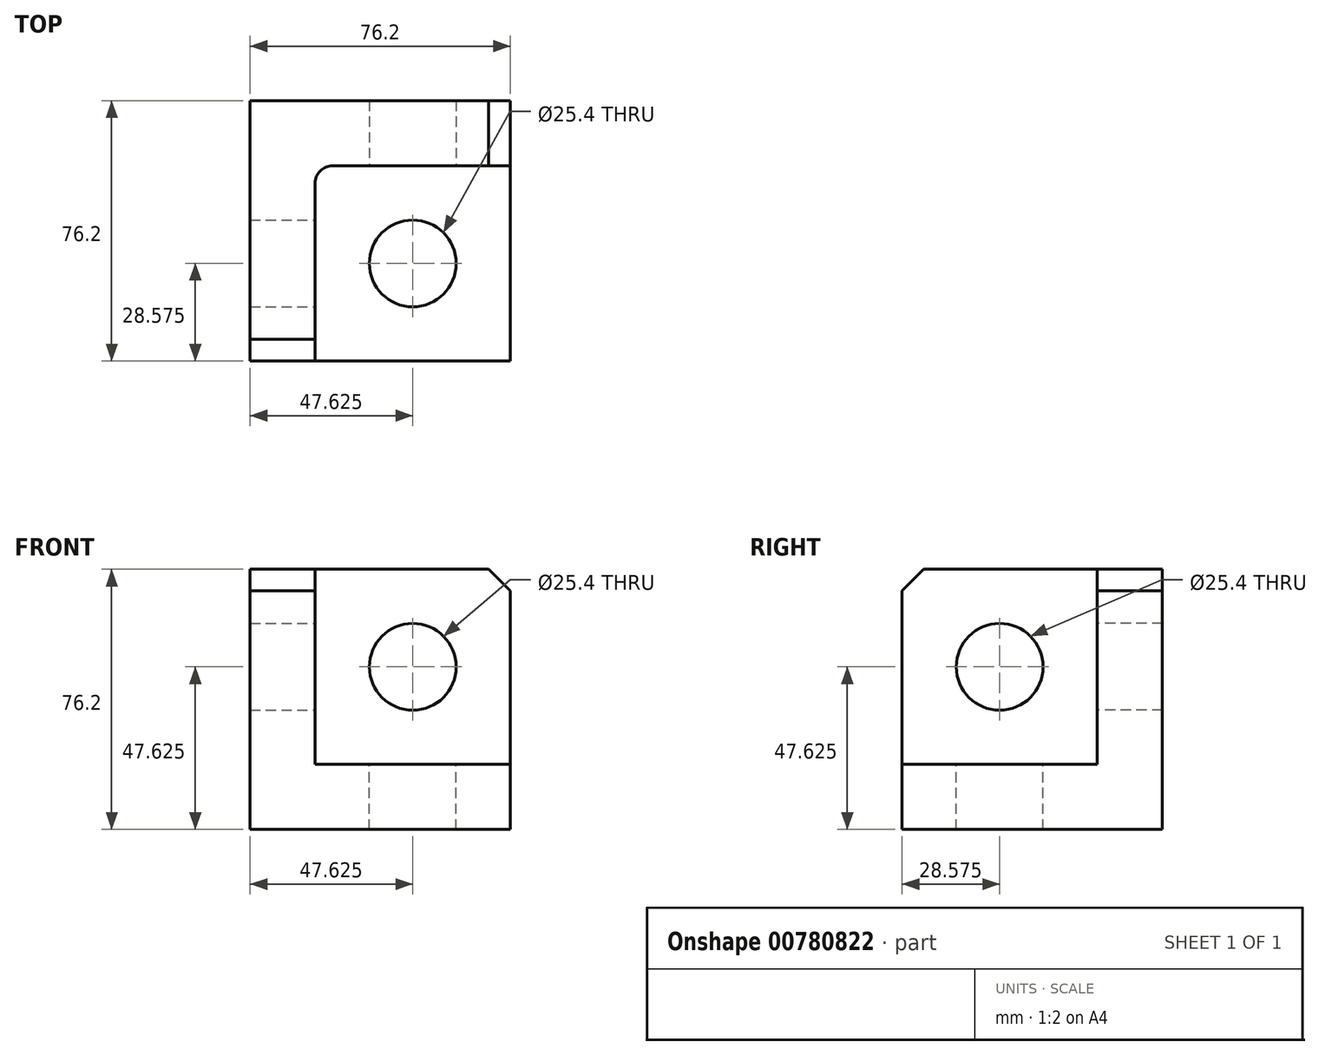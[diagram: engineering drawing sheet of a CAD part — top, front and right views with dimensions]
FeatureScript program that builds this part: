
annotation { "Feature Type Name" : "Feature", "Feature Type Description" : "" }
export const myFeature = defineFeature(function(context is Context, id is Id, definition is map)
    precondition{}
    {
        {
            var Q0;
            Q0=qCreatedBy(makeId("Front.planeOp"),FACE);
            var sketch = newSketch(context, id + "F0", { "sketchPlane" : qUnion([Q0])});
            skLineSegment(sketch, "E0.bottom", {"start": v(-38.1, 38.1) * mm, "end": v(38.1, 38.1) * mm});
            skLineSegment(sketch, "E0.top", {"start": v(-38.1, -38.1) * mm, "end": v(38.1, -38.1) * mm});
            skLineSegment(sketch, "E0.left", {"start": v(-38.1, 38.1) * mm, "end": v(-38.1, -38.1) * mm});
            skLineSegment(sketch, "E0.right", {"start": v(38.1, 38.1) * mm, "end": v(38.1, -38.1) * mm});
            skPoint(sketch, "E0.middle", {"position": v(0, 0) * mm});
            skSolve(sketch);
        }
        {
            var Q0;
            Q0=makeQuery(id+"F0.imprint","IMPRINT",FACE,{"disambiguationData":[TD([[makeQuery(id+"F0.imprint","IMPRINT",EDGE,{"derivedFrom":sQuery(id+"F0.wireOp",EDGE,"E0.bottom")}),-1.0]])]});
            extrude(context, id + "F1", {"entities" : qUnion([Q0]), "depth" : 76.2 * mm, "offsetDistance" : 25.4 * mm});
        }
        {
            var Q0;
            Q0=makeQuery(id+"F1.opExtrude","CAP_FACE",FACE,{"disambiguationData":[OSD([sQuery(id+"F0.wireOp",EDGE,"E0.bottom"),sQuery(id+"F0.wireOp",EDGE,"E0.top"),sQuery(id+"F0.wireOp",EDGE,"E0.left"),sQuery(id+"F0.wireOp",EDGE,"E0.right")])],"isStart":false});
            var sketch = newSketch(context, id + "F2", { "sketchPlane" : qUnion([Q0])});
            skLineSegment(sketch, "E1.bottom", {"start": v(38.1, 38.1) * mm, "end": v(-19.05, 38.1) * mm});
            skLineSegment(sketch, "E1.top", {"start": v(38.1, -19.05) * mm, "end": v(-19.05, -19.05) * mm});
            skLineSegment(sketch, "E1.left", {"start": v(38.1, 38.1) * mm, "end": v(38.1, -19.05) * mm});
            skLineSegment(sketch, "E1.right", {"start": v(-19.05, 38.1) * mm, "end": v(-19.05, -19.05) * mm});
            skSolve(sketch);
        }
        {
            var Q0;
            Q0=makeQuery(id+"F2.imprint","IMPRINT",FACE,{"disambiguationData":[TD([[makeQuery(id+"F2.imprint","IMPRINT",EDGE,{"derivedFrom":sQuery(id+"F2.wireOp",EDGE,"E1.bottom")}),-1.0]])]});
            extrude(context, id + "F3", {"entities" : qUnion([Q0]), "operationType" : NewBodyOperationType.REMOVE, "oppositeDirection" : true, "depth" : 57.15 * mm, "offsetDistance" : 25.4 * mm});
        }
        {
            var Q0;
            Q0=makeQuery(id+"F1.opExtrude","CAP_EDGE",EDGE,{"disambiguationData":[OSD([sQuery(id+"F0.wireOp",EDGE,"E0.bottom")])],"isStart":false});
            chamfer(context, id + "F4", {"entities" : qUnion([Q0]), "width" : 6.35 * mm, "tangentPropagation" : true});
        }
        {
            var Q0;
            Q0=makeQuery(id+"F1.opExtrude","SWEPT_EDGE",EDGE,{"disambiguationData":[OSD([sQuery(id+"F0.wireOp",EDGE,"E0.bottom"),sQuery(id+"F0.wireOp",EDGE,"E0.right")])]});
            chamfer(context, id + "F5", {"entities" : qUnion([Q0]), "width" : 6.35 * mm, "tangentPropagation" : true});
        }
        {
            var Q0;
            Q0=makeQuery(id+"F3.boolean.opBoolean","COPY",EDGE,{"derivedFrom":makeQuery(id+"F3.opExtrude","CAP_EDGE",EDGE,{"disambiguationData":[OSD([sQuery(id+"F2.wireOp",EDGE,"E1.right")])],"isStart":false})});
            fillet(context, id + "F6", {"entities" : qUnion([Q0]), "radius" : 5.08 * mm, "tangentPropagation" : true, "allowEdgeOverflow" : false});
        }
        {
            var Q0;
            Q0=makeQuery(id+"F3.boolean.opBoolean","COPY",FACE,{"derivedFrom":makeQuery(id+"F3.opExtrude","SWEPT_FACE",FACE,{"disambiguationData":[OSD([sQuery(id+"F2.wireOp",EDGE,"E1.right")])]})});
            var sketch = newSketch(context, id + "F7", { "sketchPlane" : qUnion([Q0])});
            skCircle(sketch, "E2", {"center": v(-47.62, 9.53) * mm, "radius": 12.7 * mm});
            skSolve(sketch);
        }
        {
            var Q0;
            Q0=makeQuery(id+"F7.imprint","IMPRINT",FACE,{"disambiguationData":[TD([[makeQuery(id+"F7.imprint","IMPRINT",EDGE,{"derivedFrom":sQuery(id+"F7.wireOp",EDGE,"E2")}),1.0]])]});
            extrude(context, id + "F8", {"entities" : qUnion([Q0]), "operationType" : NewBodyOperationType.REMOVE, "oppositeDirection" : true, "depth" : 19.05 * mm, "offsetDistance" : 25.4 * mm});
        }
        {
            var Q0;
            Q0=makeQuery(id+"F3.boolean.opBoolean","COPY",FACE,{"derivedFrom":makeQuery(id+"F3.opExtrude","CAP_FACE",FACE,{"disambiguationData":[OSD([sQuery(id+"F2.wireOp",EDGE,"E1.bottom"),sQuery(id+"F2.wireOp",EDGE,"E1.top"),sQuery(id+"F2.wireOp",EDGE,"E1.left"),sQuery(id+"F2.wireOp",EDGE,"E1.right")])],"isStart":false})});
            var sketch = newSketch(context, id + "F9", { "sketchPlane" : qUnion([Q0])});
            skCircle(sketch, "E3", {"center": v(9.53, 9.52) * mm, "radius": 12.7 * mm});
            skSolve(sketch);
        }
        {
            var Q0;
            Q0=makeQuery(id+"F9.imprint","IMPRINT",FACE,{"disambiguationData":[TD([[makeQuery(id+"F9.imprint","IMPRINT",EDGE,{"derivedFrom":sQuery(id+"F9.wireOp",EDGE,"E3")}),1.0]])]});
            extrude(context, id + "F10", {"entities" : qUnion([Q0]), "operationType" : NewBodyOperationType.REMOVE, "oppositeDirection" : true, "depth" : 19.05 * mm, "offsetDistance" : 25.4 * mm});
        }
        {
            var Q0;
            Q0=makeQuery(id+"F3.boolean.opBoolean","COPY",FACE,{"derivedFrom":makeQuery(id+"F3.opExtrude","SWEPT_FACE",FACE,{"disambiguationData":[OSD([sQuery(id+"F2.wireOp",EDGE,"E1.top")])]})});
            var sketch = newSketch(context, id + "F11", { "sketchPlane" : qUnion([Q0])});
            skCircle(sketch, "E4", {"center": v(9.53, -47.62) * mm, "radius": 12.7 * mm});
            skSolve(sketch);
        }
        {
            var Q0;
            Q0=makeQuery(id+"F11.imprint","IMPRINT",FACE,{"disambiguationData":[TD([[makeQuery(id+"F11.imprint","IMPRINT",EDGE,{"derivedFrom":sQuery(id+"F11.wireOp",EDGE,"E4")}),1.0]])]});
            extrude(context, id + "F12", {"entities" : qUnion([Q0]), "operationType" : NewBodyOperationType.REMOVE, "oppositeDirection" : true, "depth" : 19.05 * mm, "offsetDistance" : 25.4 * mm});
        }
    });
